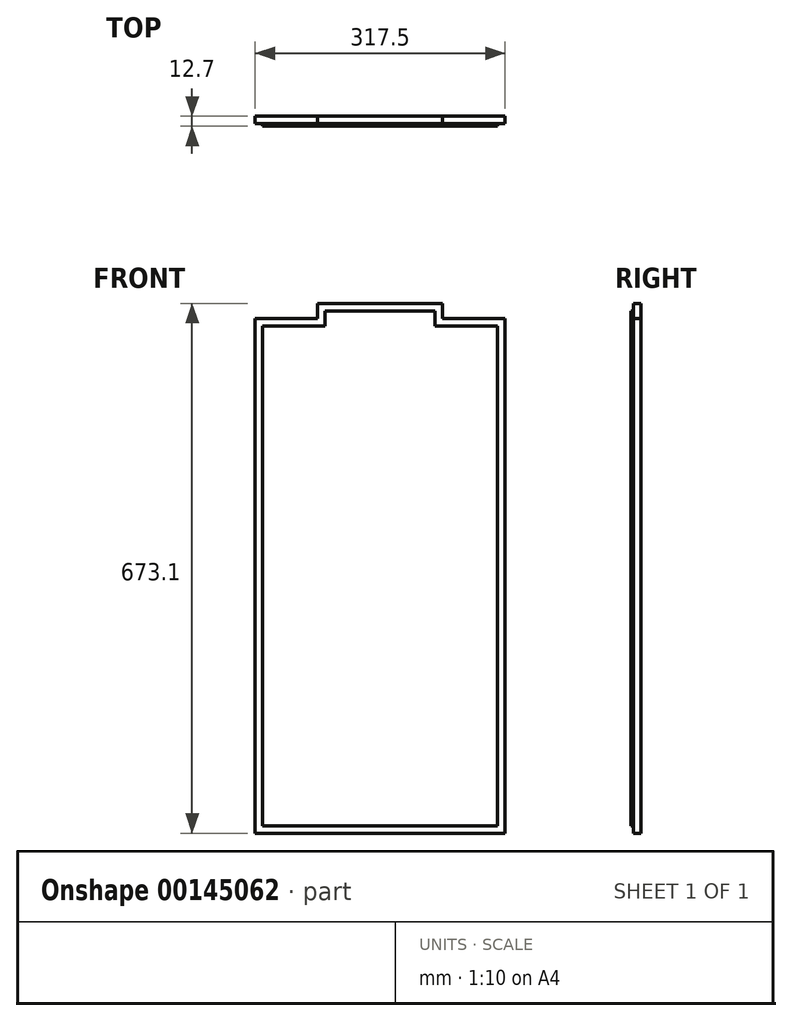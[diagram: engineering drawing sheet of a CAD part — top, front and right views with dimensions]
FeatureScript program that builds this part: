
annotation { "Feature Type Name" : "Feature", "Feature Type Description" : "" }
export const myFeature = defineFeature(function(context is Context, id is Id, definition is map)
    precondition{}
    {
        {
            var Q0;
            Q0=qCreatedBy(makeId("Front.planeOp"),FACE);
            var sketch = newSketch(context, id + "F0", { "sketchPlane" : qUnion([Q0])});
            skLineSegment(sketch, "E0.bottom", {"start": v(0, 0) * mm, "end": v(317.5, 0) * mm});
            skLineSegment(sketch, "E0.top", {"start": v(79.37, 673.1) * mm, "end": v(238.12, 673.1) * mm});
            skLineSegment(sketch, "E0.left", {"start": v(0, 0) * mm, "end": v(0, 654.05) * mm});
            skLineSegment(sketch, "E0.right", {"start": v(317.5, 0) * mm, "end": v(317.5, 654.05) * mm});
            skLineSegment(sketch, "E1.top", {"start": v(0, 654.05) * mm, "end": v(79.37, 654.05) * mm});
            skLineSegment(sketch, "E2.left", {"start": v(79.37, 673.1) * mm, "end": v(79.37, 654.05) * mm});
            skLineSegment(sketch, "E2.right", {"start": v(238.12, 673.1) * mm, "end": v(238.12, 654.05) * mm});
            skLineSegment(sketch, "E3.top", {"start": v(88.9, 663.58) * mm, "end": v(228.6, 663.58) * mm});
            skLineSegment(sketch, "E4", {"start": v(88.9, 663.58) * mm, "end": v(88.9, 644.52) * mm});
            skLineSegment(sketch, "E5", {"start": v(88.9, 644.52) * mm, "end": v(9.52, 644.52) * mm});
            skLineSegment(sketch, "E6", {"start": v(9.52, 644.52) * mm, "end": v(9.52, 9.53) * mm});
            skLineSegment(sketch, "E7", {"start": v(9.52, 9.52) * mm, "end": v(307.98, 9.52) * mm});
            skLineSegment(sketch, "E8", {"start": v(307.98, 9.53) * mm, "end": v(307.97, 644.52) * mm});
            skLineSegment(sketch, "E9", {"start": v(228.6, 663.58) * mm, "end": v(228.6, 644.52) * mm});
            skLineSegment(sketch, "E10", {"start": v(228.6, 644.52) * mm, "end": v(307.97, 644.52) * mm});
            skLineSegment(sketch, "E11.trimOffspring", {"start": v(238.12, 654.05) * mm, "end": v(317.5, 654.05) * mm});
            skSolve(sketch);
        }
        {
            var Q0;
            Q0=makeQuery(id+"F0.imprint","IMPRINT",FACE,{"disambiguationData":[TD([[makeQuery(id+"F0.imprint","IMPRINT",EDGE,{"derivedFrom":sQuery(id+"F0.wireOp",EDGE,"E3.top")}),-1.0]])]});
            extrude(context, id + "F1", {"entities" : qUnion([Q0]), "depth" : 12.7 * mm});
        }
        {
            var Q0;
            Q0=makeQuery(id+"F0.imprint","IMPRINT",FACE,{"disambiguationData":[TD([[makeQuery(id+"F0.imprint","IMPRINT",EDGE,{"derivedFrom":sQuery(id+"F0.wireOp",EDGE,"E0.bottom")}),1.0]])]});
            extrude(context, id + "F2", {"entities" : qUnion([Q0]), "operationType" : NewBodyOperationType.ADD, "depth" : 9.52 * mm});
        }
    });
